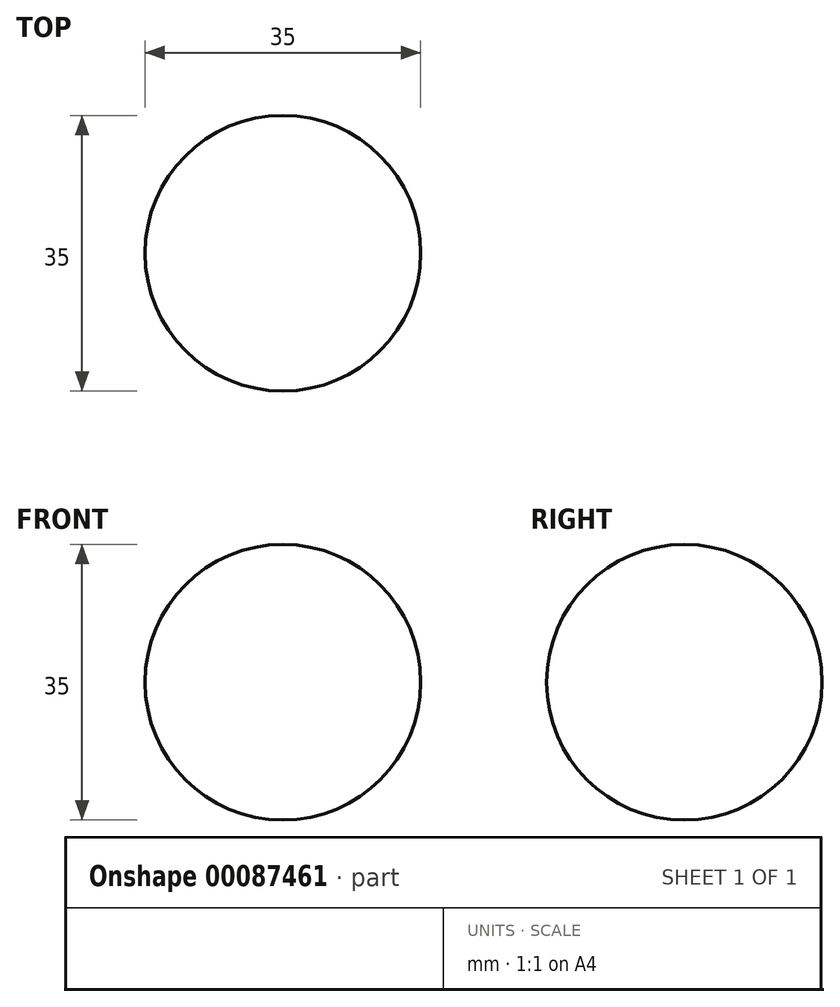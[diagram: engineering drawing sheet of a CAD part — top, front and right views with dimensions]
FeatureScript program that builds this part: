
annotation { "Feature Type Name" : "Feature", "Feature Type Description" : "" }
export const myFeature = defineFeature(function(context is Context, id is Id, definition is map)
    precondition{}
    {
        {
            var Q0;
            Q0=qCreatedBy(makeId("Front.planeOp"),FACE);
            var sketch = newSketch(context, id + "F0", { "sketchPlane" : qUnion([Q0])});
            skLineSegment(sketch, "E0", {"start": v(0, -17.5) * mm, "end": v(0, 17.5) * mm});
            skArc(sketch, "E1", {"start": v(0, 17.5) * mm, "mid": v(-17.5, 0) * mm, "end": v(0, -17.5) * mm});
            skSolve(sketch);
        }
        {
            var Q0;
            Q0=makeQuery(id+"F0.imprint","IMPRINT",FACE,{"disambiguationData":[TD([[makeQuery(id+"F0.imprint","IMPRINT",EDGE,{"derivedFrom":sQuery(id+"F0.wireOp",EDGE,"E0")}),1.0]])]});
            var Q1;
            Q1=sQuery(id+"F0.wireOp",EDGE,"E0");
            revolve(context, id + "F1", {"entities" : qUnion([Q0]), "axis" : qUnion([Q1]), "revolveType" : RevolveType.FULL});
        }
    });
